# Revit family: GIRA_1239600
name_source: partatom
category: Elektroinstallationen
revit_build: Autodesk Revit 2017 (Build: 20160225_1515(x64)
units: mm (PartAtom-declared; Revit-internal decimal feet)

## family parameters
Basisbauteil = Fläche
Beim Laden mit Abzugskörper schneiden = Nein
Bemaßung runder Anschluss = Durchmesser verwenden
Beschriftungsausrichtung beibehalten = Ja
Gemeinsam genutzt = Nein
Raumberechnungspunkt = Nein
Teiletyp = Normal

## types (1)
- GIRA_1239600
    Abhörsicher = Ja
    BIM = https://media.stage.bim.site 600.rfa
    Bedienung Türöffner = Ja
    Beschreibung = Wohnungsstation Video AP Plus System 55 Edelstahl (lackiert) Merkmale: - Bei Verwendung je einer Spannungsversorgung für Türkommunikation können bis zu 28 Wohnungsstationen Video AP parallel genutzt werden. - Die Wohnungsstation Video AP Plus erkennt automatisch, ob eine Spannungsversorgung für Türkommunikation angeschlossen ist. Eine Brücke zwischen ZV und BUS ist nicht notwendig. - Farbdisplay mit LED-Hintergrundbeleuchtung. - OSD Funktion, d. h. Texteinblendung im Display zur Statusanzeige und Menüführung. - Kapazitive Bedientasten mit integrierten Leuchtdioden zur Zustandsanzeige: Die Tasten werden durch leichte Berührung bedient. - Zuschaltbare Türöffnerautomatik: bei eingeschalteter Funktion wird der Türöffner nach Betätigung der Türstationsruftaste automatisch angesteuert. - Automatische Rufannahme: direktes Hineinsprechen oder -hören in einen Raum nach Internruf. - Gebührenfreier hausinterner Sprechverkehr mit bis zu zehn weiteren Wohnungsstationen. Die Bedientasten der Wohnungsstation Video AP Plus steuern die folgenden Funktionen:: - Manuelles Ein- und Ausschalten des TFT-Farbdisplays. - Kameraumschaltung - gezielte Anwahl der angeschlossenen Farbkameras. Im Display erfolgt die Textanzeige, welche Kamera aktuell angesteuert wird. - Schalten von Licht und anderen Funktionen in Verbindung mit dem Schaltaktor oder dem Unterputz-Schaltaktor. - Ansteuerung des Türöffners. - Rufton ein- und ausschalten. - Rufannahme. - Aktivierung der Durchsetzfunktion. - Einstellung von Rufton- und Sprechlautstärke. Funktionen im Endkundenmenü: - Internruf, Schalthandlung, Ruftonmelodie, Helligkeit, Farbsättigung, Kontrast, Einschaltzeit des Displays, Sprache (21 Sprachen wählbar), Tastentöne, Türöffnerautomatik (nach Installateurfreigabe), automatische Rufannahme (nach Installateurfreigabe). Zusätzliche Funktionen im Installateurmenü:: - Einstellung Haupt- Nebendisplay, Frequenzeinstellung, Terminierung der Leitung, Versionsanzeige, Werkseinstellung, Display ein- bzw. ausschalten, LED-Beleuchtung ein- bzw. ausschalten, Ruftastenzuordnung, Internruf zuordnen, Freigaben für Türöffnerautomatik und automatische Rufannahme. - Karten-Slot für SD-Speicherkarte. - SD-Speicherkarte. Neue zusätzliche Funktionen im Endkundenmenü:: - Interner Bildspeicher (nach Installateurfreigabe) für bis zu 48 Bilder. Manueller Übertrag interner zu externner Bildspeicher (SD-Speicherkarte). Bildspeicher manuell löschen. Manuellen Schnappschuss auslösen. Schalthandlungen und Internrufe umbenennen. Datum Uhrzeit ändern. Neue zusätzliche Funktionen im Installateurmenü:: - Freigabe des internen Bildspeichers. Einstellen des Bildintervals und der Aufnahmegeschwindigkeit. Datum Uhrzeit einstellen. Eigenschaften der SD-Speicherkarte:: - Verzeichnis für zehn Klingeltöne, davon fünf frei konfigurierbar im WAVE-Format. Ordner für externen Bildspeicher (max. 200 Bilder).  Hinweise : - Montage ohne Abdeckrahmen oder mit Abdeckrahmen 2fach ohne Mittelsteg aus den Schalterprogrammen System 55, Flächenschalter oder Gira E22 möglich.
    Bildsystem = PAL
    Funktions-Lampen = Ja
    GTIN = 4010337035992
    HAN = 1239600
    Hersteller = Gira
    Hörgerätekompatibel = Nein
    Internkommunikation = Ja
    Ist System = Nein
    Ist Zubehör = Nein
    Lautstärkeregelung = Ja
    Mit Touchscreen = Nein
    Mit Türöffnerautomatik = Ja
    Rufabschaltung = Ja
    Rufunterscheidung = Ja
    Schaltfunktionen = Ja
    Typname = Wohnungsstation Video AP Plus System 55 Edelstahl(lack.)
    URL = https://www.gira.de
    Verbindung mit Smartphone möglich = Nein
    Vorgabe-Ansicht = 1219 mm
    Zusatzgerät anreihbar = Nein

## geometry (parser evidence)
native form markers: Sweep x2
no freeform markers — native parametric forms only
